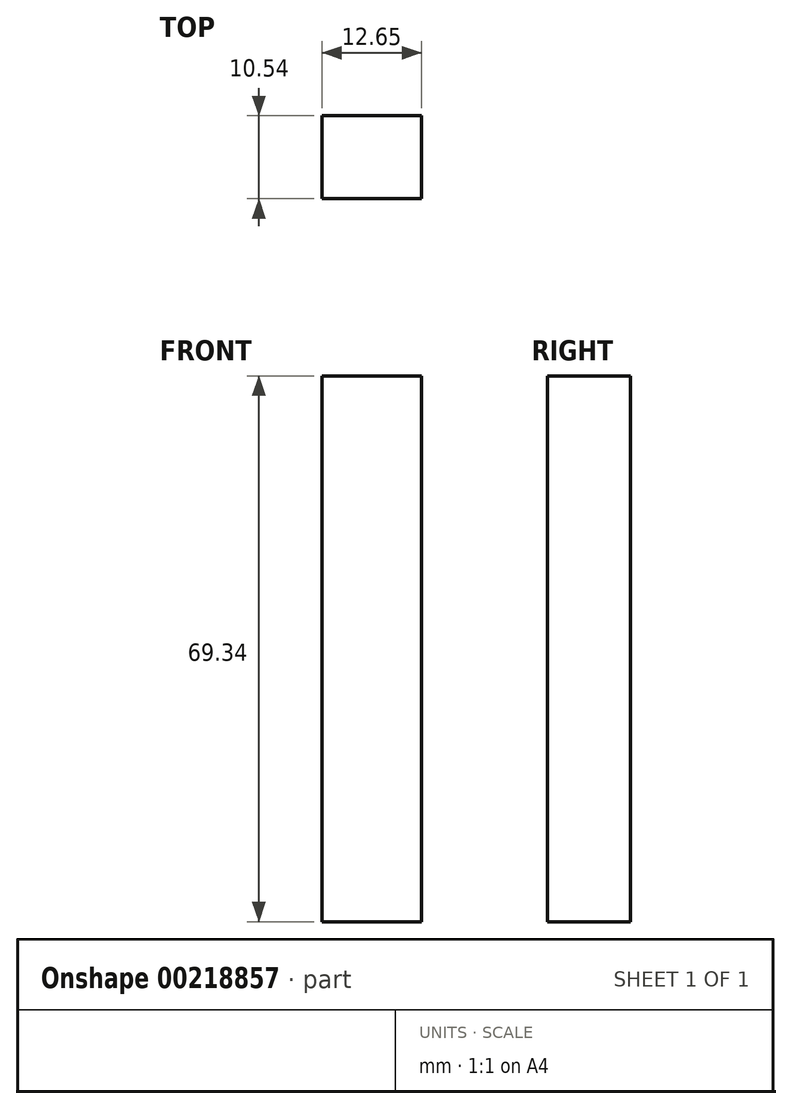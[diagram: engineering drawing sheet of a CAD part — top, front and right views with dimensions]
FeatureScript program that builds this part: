
annotation { "Feature Type Name" : "Feature", "Feature Type Description" : "" }
export const myFeature = defineFeature(function(context is Context, id is Id, definition is map)
    precondition{}
    {
        {
            var Q0;
            Q0=qCreatedBy(makeId("Top.planeOp"),FACE);
            var sketch = newSketch(context, id + "F0", { "sketchPlane" : qUnion([Q0])});
            skLineSegment(sketch, "E0.bottom", {"start": v(0, 0) * mm, "end": v(12.65, 0) * mm});
            skLineSegment(sketch, "E0.top", {"start": v(0, -10.54) * mm, "end": v(12.65, -10.54) * mm});
            skLineSegment(sketch, "E0.left", {"start": v(0, 0) * mm, "end": v(0, -10.54) * mm});
            skLineSegment(sketch, "E0.right", {"start": v(12.65, 0) * mm, "end": v(12.65, -10.54) * mm});
            skSolve(sketch);
        }
        {
            var Q0;
            Q0=makeQuery(id+"F0.imprint","IMPRINT",FACE,{"disambiguationData":[TD([[makeQuery(id+"F0.imprint","IMPRINT",EDGE,{"derivedFrom":sQuery(id+"F0.wireOp",EDGE,"E0.bottom")}),-1.0]])]});
            extrude(context, id + "F1", {"entities" : qUnion([Q0]), "depth" : 69.34 * mm});
        }
    });
